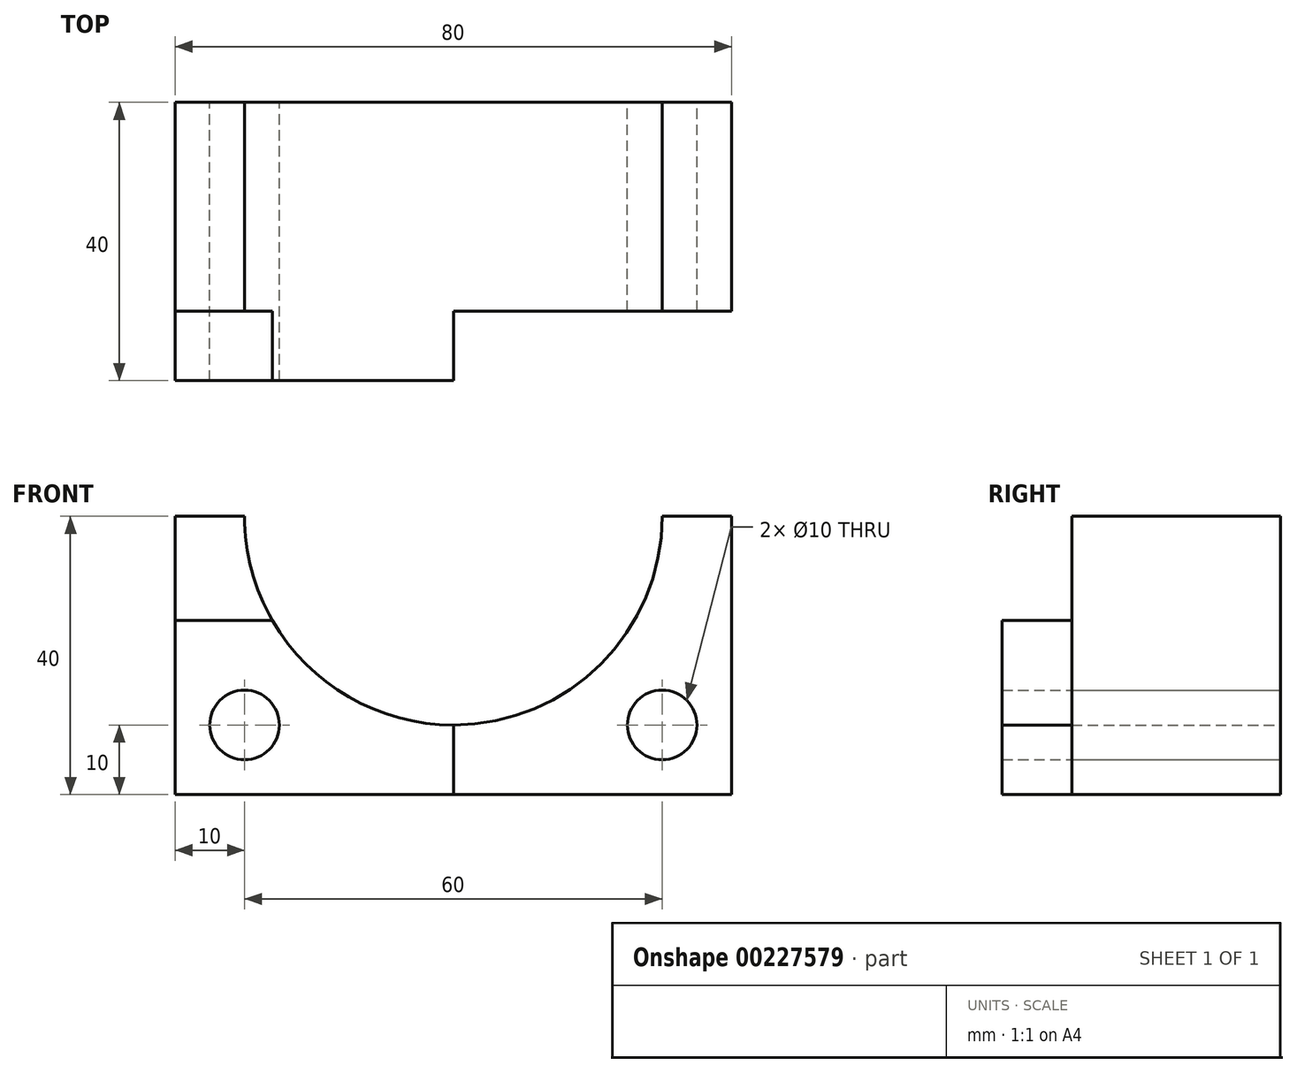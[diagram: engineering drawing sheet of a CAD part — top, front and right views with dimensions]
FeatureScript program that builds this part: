
annotation { "Feature Type Name" : "Feature", "Feature Type Description" : "" }
export const myFeature = defineFeature(function(context is Context, id is Id, definition is map)
    precondition{}
    {
        {
            var Q0;
            Q0=qCreatedBy(makeId("Front.planeOp"),FACE);
            var sketch = newSketch(context, id + "F0", { "sketchPlane" : qUnion([Q0])});
            skLineSegment(sketch, "E0.bottom", {"start": v(0, 0) * mm, "end": v(80, 0) * mm});
            skLineSegment(sketch, "E0.top", {"start": v(0, 40) * mm, "end": v(10, 40) * mm});
            skLineSegment(sketch, "E0.left", {"start": v(0, 0) * mm, "end": v(0, 40) * mm});
            skLineSegment(sketch, "E0.right", {"start": v(80, 0) * mm, "end": v(80, 40) * mm});
            skLineSegment(sketch, "E1", {"start": v(80, 40) * mm, "end": v(70, 40) * mm});
            skArc(sketch, "E2", {"start": v(10, 40) * mm, "mid": v(40, 10) * mm, "end": v(70, 40) * mm});
            skLineSegment(sketch, "E3.trimOffspring", {"start": v(70, 40) * mm, "end": v(80, 40) * mm});
            skLineSegment(sketch, "E4", {"start": v(40, 10) * mm, "end": v(40, 0) * mm});
            skLineSegment(sketch, "E5", {"start": v(0, 25) * mm, "end": v(14.02, 25) * mm});
            skCircle(sketch, "E6", {"center": v(70, 10) * mm, "radius": 5 * mm});
            skCircle(sketch, "E7", {"center": v(10, 10) * mm, "radius": 5 * mm});
            skSolve(sketch);
        }
        {
            var Q0;
            Q0 = qSketchRegion(id + "F0", true);
            extrude(context, id + "F1", {"entities" : qUnion([Q0]), "depth" : 30 * mm});
        }
        {
            var Q0;
            {var subQ0=sQuery(id+"F0.wireOp",EDGE,"E4");Q0=makeQuery(id+"F0.imprint","IMPRINT",FACE,{"disambiguationData":[TD([[makeQuery(id+"F0.imprint","IMPRINT",EDGE,{"derivedFrom":subQ0}),-1.0]])]});}
            extrude(context, id + "F2", {"entities" : qUnion([Q0]), "operationType" : NewBodyOperationType.ADD, "depth" : 40 * mm});
        }
    });
